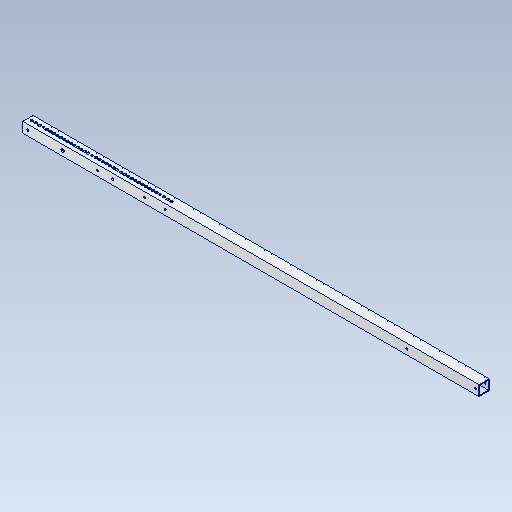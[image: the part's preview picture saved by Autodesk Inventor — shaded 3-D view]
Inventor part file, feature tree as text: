
AUTODESK INVENTOR PART (.ipt)
format: ipt  version: 2020.3 (Build 243373000, 373)  size: 286,208 bytes
history: native  units: mm
features: sketch x11, hole x8, extrude x3, other x1
ambient origin geometry x8: Origin, YZ Plane, XZ Plane, XY Plane, X Axis, Y Axis, Z Axis, Center Point
bodies: Body1 (feature_tree)
feature tree (23):
  other  "ソリッド1"
  extrude  "押し出し1"  Depth=15.0mm
  hole  "穴1"  [1 undecoded]
  hole  "穴2"  [1 undecoded]
  hole  "穴3"  [1 undecoded]
  extrude  "押し出し2"  Depth=1.2mm
  hole  "穴4"  [1 undecoded]
  hole  "穴5"  [1 undecoded]
  hole  "穴6"  [1 undecoded]
  hole  "穴7"  [1 undecoded]
  extrude  "押し出し3"  Depth=7.5mm
  hole  "穴8"  [1 undecoded]
  sketch  "スケッチ1"
  sketch  "スケッチ2"
  sketch  "スケッチ3"
  sketch  "スケッチ4"
  sketch  "スケッチ5"
  sketch  "スケッチ6"
  sketch  "スケッチ7"
  sketch  "スケッチ8"
  sketch  "スケッチ9"
  sketch  "スケッチ11"
  sketch  "スケッチ12"
note: 8 required parameter values undecoded (feature->parameter linkage not recoverable at this tier; creation-order binding heuristic only, values carry confidence <= 0.55)
